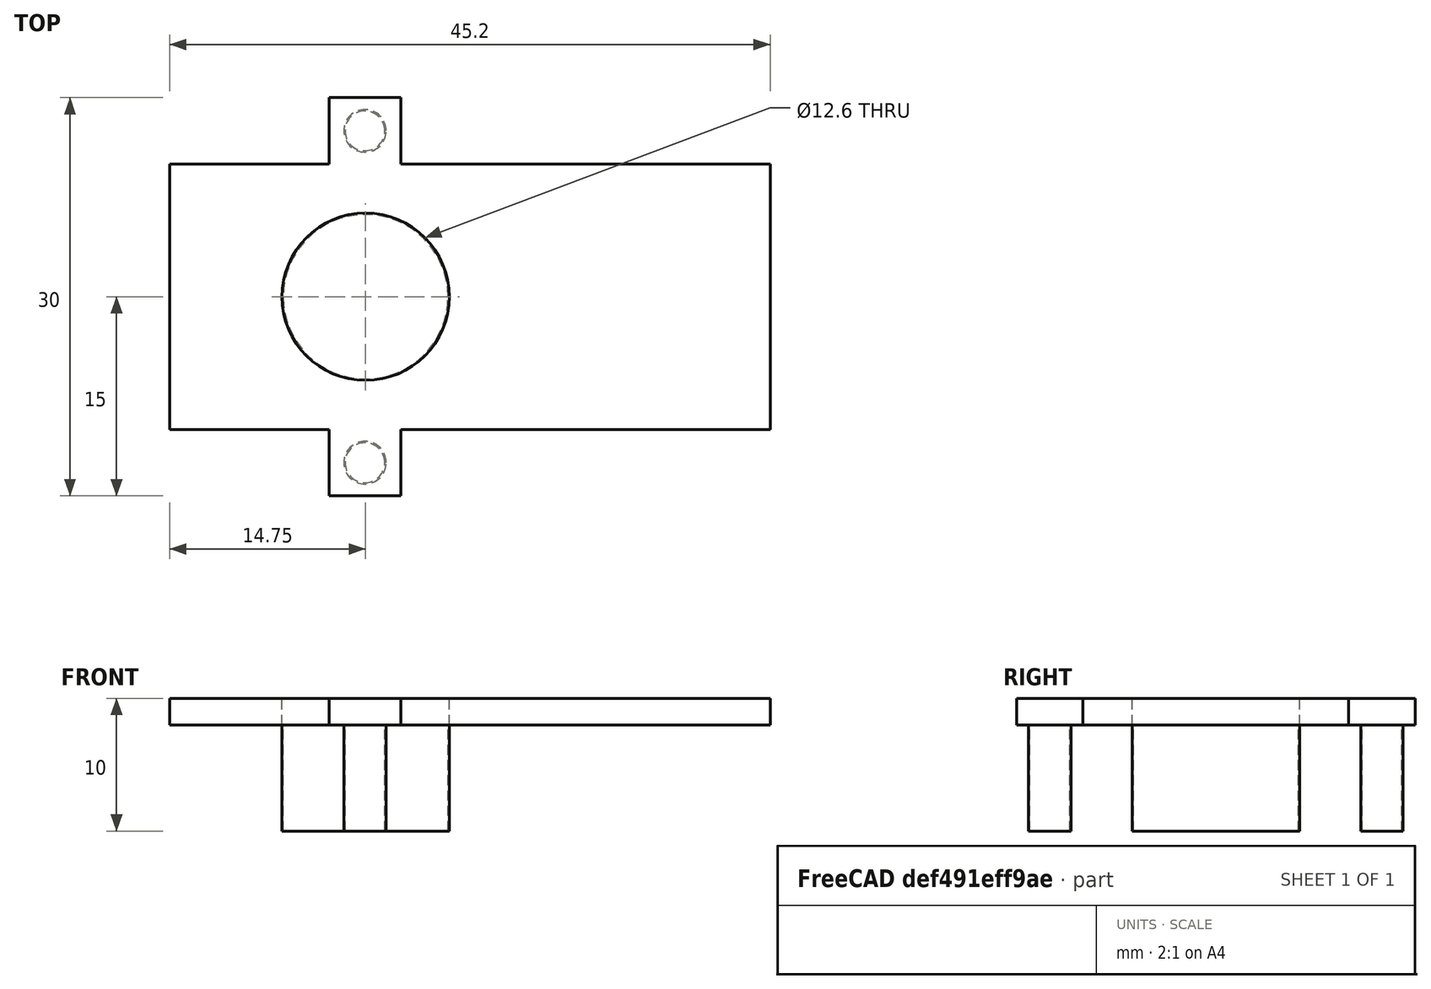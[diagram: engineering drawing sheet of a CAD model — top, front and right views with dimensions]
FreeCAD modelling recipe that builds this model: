
FCSTD DOCUMENT  (FreeCAD 0.17R13522 (Git))
Label: perforador_para_doble_encoder
License: All rights reserved
LicenseURL: http://en.wikipedia.org/wiki/All_rights_reserved
objects: Part::Fuse×4, Part::Cylinder×3, Part::Box×3, Part::FeaturePython×1, Part::Feature×1
note: 12 computed .brp shape members not serialized (recipe doc carries the construction recipe); baked Part::Feature solids carry a one-line shape summary decoded from their .brp

FEATURE [Part::Cylinder] Cylinder  label="taladro1"
  Angle = 360
  AttacherType = Attacher::AttachEngine3D
  Height = 10
  Placement = pos=(-7.9,-12.5,-6) rot=(0,0,1;0rad)
  Radius = 1.6
FEATURE [Part::Cylinder] Cylinder001  label="taladro2"
  Angle = 360
  AttacherType = Attacher::AttachEngine3D
  Height = 10
  Placement = pos=(-7.9,12.5,-6) rot=(0,0,1;0rad)
  Radius = 1.6
FEATURE [Part::Box] Box  label="base"
  AttacherType = Attacher::AttachEngine3D
  Height = 2
  Length = 45.2
  Placement = pos=(-22.6,-10,2) rot=(0,0,1;0rad)
  Width = 20
FEATURE [Part::Box] Box001  label="oreja2"
  AttacherType = Attacher::AttachEngine3D
  Height = 2
  Length = 5.4
  Placement = pos=(-10.6,10,2) rot=(0,0,1;0rad)
  Width = 5
FEATURE [Part::Box] Box002  label="oreja1"
  AttacherType = Attacher::AttachEngine3D
  Height = 2
  Length = 5.4
  Placement = pos=(-10.6,-15,2) rot=(0,0,1;0rad)
  Width = 5
FEATURE [Part::Fuse] Fusion
  Base = -> Box
  Tool = -> Box002
FEATURE [Part::Fuse] Fusion001
  Base = -> Box001
  Tool = -> Fusion
FEATURE [Part::Fuse] Fusion002
  Base = -> Cylinder
  Tool = -> Fusion001
FEATURE [Part::Fuse] Fusion003  label="posicionador encoder doble"
  Base = -> Cylinder001
  Placement = pos=(0,0,-4) rot=(0,0,1;0rad)
  Tool = -> Fusion002
FEATURE [Part::Cylinder] Cylinder002  label="engranaje-bastago-grande"
  Angle = 360
  AttacherType = Attacher::AttachEngine3D
  Height = 10
  Placement = pos=(-7.85,0,-10) rot=(0,0,1;0rad)
  Radius = 6.3
FEATURE [Part::FeaturePython] BooleanFragments  label="posicion_encoder_doble"  # WARN: FeaturePython — macro-defined, semantics opaque (R4)
  Mode = 0
  Objects = -> [Fusion003,Cylinder002]
  Tolerance = 0
FEATURE [Part::Feature] BooleanFragments_solid  label="posicion_encoder_doble (Solid)"
  shape: bbox 45.2 x 30 x 10 mm, 29 faces (baked)
